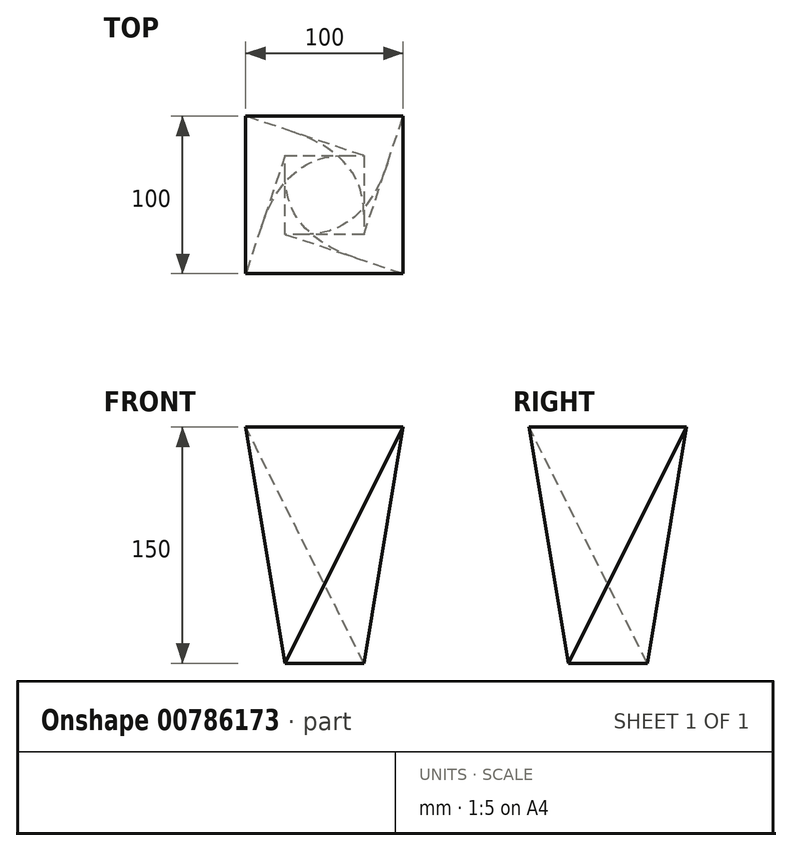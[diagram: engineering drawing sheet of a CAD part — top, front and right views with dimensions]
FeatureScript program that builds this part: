
annotation { "Feature Type Name" : "Feature", "Feature Type Description" : "" }
export const myFeature = defineFeature(function(context is Context, id is Id, definition is map)
    precondition{}
    {
        {
            var Q0;
            Q0=qCreatedBy(makeId("Top.planeOp"),FACE);
            var sketch = newSketch(context, id + "F0", { "sketchPlane" : qUnion([Q0])});
            skCircle(sketch, "E0.cCircle", {"center": v(0, 0) * mm, "radius": 25 * mm, "construction": true});
            skLineSegment(sketch, "E0.0", {"start": v(25, 25) * mm, "end": v(25, -25) * mm});
            skLineSegment(sketch, "E0.1", {"start": v(25, -25) * mm, "end": v(-25, -25) * mm});
            skLineSegment(sketch, "E0.2", {"start": v(-25, -25) * mm, "end": v(-25, 25) * mm});
            skLineSegment(sketch, "E0.3", {"start": v(-25, 25) * mm, "end": v(25, 25) * mm});
            skPoint(sketch, "E0.0.midPoint", {"position": v(25, 0) * mm});
            skSolve(sketch);
        }
        {
            var Q0;
            Q0=qCreatedBy(makeId("Top.planeOp"),FACE);
            cPlane(context, id + "F1", {"entities" : qUnion([Q0]), "cplaneType" : CPlaneType.OFFSET, "offset" : 150 * mm, "width" : 150 * mm, "height" : 150 * mm});
        }
        {
            var Q0;
            Q0=qCreatedBy(id+"F1.planeOp",FACE);
            var sketch = newSketch(context, id + "F2", { "sketchPlane" : qUnion([Q0])});
            skCircle(sketch, "E1.cCircle", {"center": v(0, 0) * mm, "radius": 50 * mm, "construction": true});
            skLineSegment(sketch, "E1.0", {"start": v(50, 50) * mm, "end": v(50, -50) * mm});
            skLineSegment(sketch, "E1.1", {"start": v(50, -50) * mm, "end": v(-50, -50) * mm});
            skLineSegment(sketch, "E1.2", {"start": v(-50, -50) * mm, "end": v(-50, 50) * mm});
            skLineSegment(sketch, "E1.3", {"start": v(-50, 50) * mm, "end": v(50, 50) * mm});
            skPoint(sketch, "E1.0.midPoint", {"position": v(50, 0) * mm});
            skSolve(sketch);
        }
        {
            var Q0;
            Q0=makeQuery(id+"F0.imprint","IMPRINT",FACE,{"disambiguationData":[TD([[makeQuery(id+"F0.imprint","IMPRINT",EDGE,{"derivedFrom":sQuery(id+"F0.wireOp",EDGE,"E0.0")}),-1.0]])]});
            var Q1;
            Q1=makeQuery(id+"F2.imprint","IMPRINT",FACE,{"disambiguationData":[TD([[makeQuery(id+"F2.imprint","IMPRINT",EDGE,{"derivedFrom":sQuery(id+"F2.wireOp",EDGE,"E1.0")}),-1.0]])]});
            var Q2;
            Q2=sQuery(id+"F0.wireOp",VERTEX,"E0.0.start");
            var Q3;
            Q3=sQuery(id+"F2.wireOp",VERTEX,"E1.2.end");
            loft(context, id + "F3", {"sheetProfilesArray" : [{ "sheetProfileEntities" : qUnion([Q0]) }, { "sheetProfileEntities" : qUnion([Q1]) }], "matchConnections" : true, "connections" : [{ "connectionEntities" : qUnion([Q2, Q3]), "connectionEdgeQueries" : qUnion([]), "connectionEdgeParameters" : [] }]});
        }
    });
